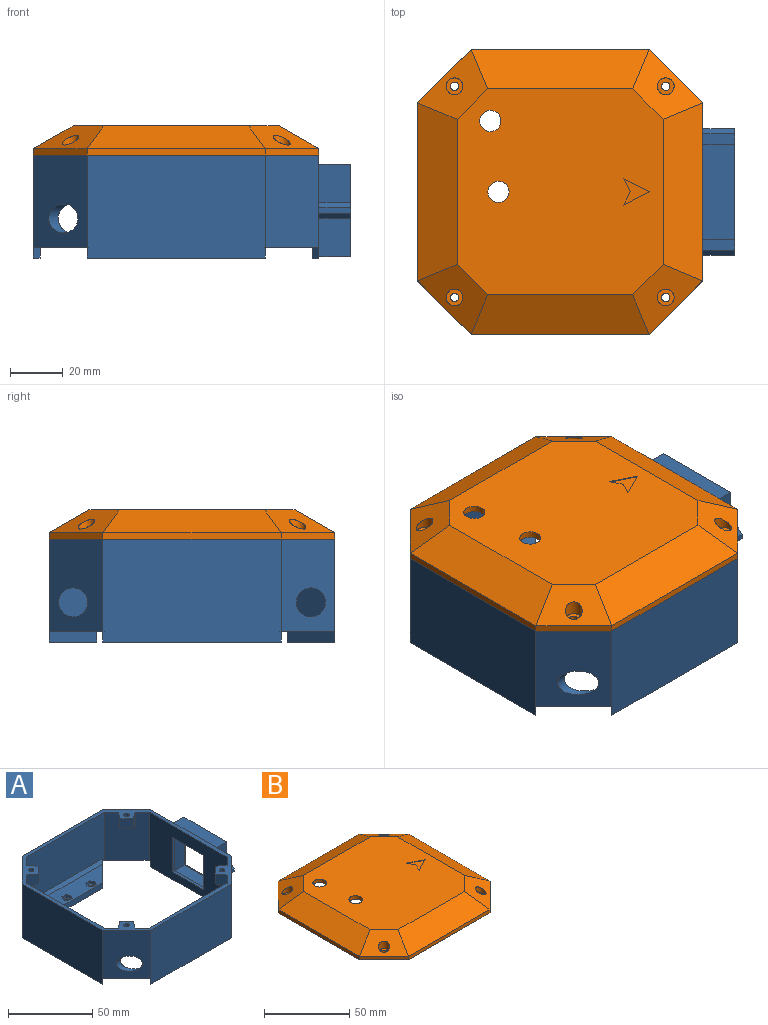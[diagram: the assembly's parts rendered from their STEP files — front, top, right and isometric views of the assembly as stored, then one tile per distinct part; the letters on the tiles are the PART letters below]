
ASSEMBLY  parts=2 mates=1
PART A: 156 faces, bbox 120x108x39 mm
  f0: plane 35x18.85mm, normal (-0.71,0.71,0), area 833.2mm2, adj f14,f20,f25,f28,f143,f144,f153
  f1: plane 35x18.85mm, normal (0.71,0.71,0), area 698.8mm2, adj f12,f20,f27,f28,f29,f131,f132,f141
  f2: plane 35x18.85mm, normal (0.71,-0.71,0), area 698.8mm2, adj f15,f20,f26,f27,f30,f119,f120,f129
  f3: plane 35x18.85mm, normal (-0.71,-0.71,0), area 833.2mm2, adj f13,f20,f25,f26,f107,f108,f117
  f4: cylinder r=1.6mm len=3.2mm, axis (0,0,1), area 20.1mm2, adj f34,f98
  f5: cylinder r=1.6mm len=3.2mm, axis (0,0,1), area 20.1mm2, adj f34,f99
  f6: cylinder r=1.6mm len=3.2mm, axis (0,0,1), area 20.1mm2, adj f40,f85
  f7: cylinder r=1.6mm len=3.2mm, axis (0,0,1), area 20.1mm2, adj f40,f84
  f8: plane 26x2mm, normal (0,0,-1), area 52mm2, adj f9,f10,f25,f51
  f9: plane 25x2mm, normal (0,-1,0), area 50mm2, adj f8,f11,f25,f51
  f10: plane 25x2mm, normal (0,1,0), area 50mm2, adj f8,f11,f25,f51
  f11: plane 26x2mm, normal (0,0,1), area 52mm2, adj f9,f10,f25,f51
  f12: plane 22.82x22.82mm, normal (0,0,-1), area 72.9mm2, adj f1,f24,f27,f28,f32,f44
  f13: plane 22.82x22.82mm, normal (0,0,-1), area 72.9mm2, adj f3,f22,f25,f26,f38,f42
  f14: plane 22.82x22.82mm, normal (0,0,-1), area 72.9mm2, adj f0,f23,f25,f28,f31,f41
  f15: plane 22.82x22.82mm, normal (0,0,-1), area 72.9mm2, adj f2,f21,f26,f27,f37,f45
  f16: plane 67.36x39mm, normal (1,0,0), area 1303.1mm2, adj f20,f22,f23,f41,f42,f43,f57,f58
  f17: plane 67.36x39mm, normal (0,1,0), area 2627.1mm2, adj f20,f21,f22,f37,f38,f40
  f18: plane 67.36x39mm, normal (-1,0,0), area 2627.1mm2, adj f20,f21,f24,f44,f45,f46
  f19: plane 67.36x39mm, normal (0,-1,0), area 2627.1mm2, adj f20,f23,f24,f31,f32,f34
  f20: plane 108x108mm, normal (0,0,1), area 1160.1mm2, adj f0,f1,f2,f3,f16,f17,f18,f19
  f21: plane 35x20.32mm, normal (-0.71,0.71,0), area 871.3mm2, adj f15,f17,f18,f20,f30
  f22: plane 35x20.32mm, normal (0.71,0.71,0), area 1005.7mm2, adj f13,f16,f17,f20
  f23: plane 35x20.32mm, normal (0.71,-0.71,0), area 1005.7mm2, adj f14,f16,f19,f20
  f24: plane 35x20.32mm, normal (-0.71,-0.71,0), area 871.3mm2, adj f12,f18,f19,f20,f29
  f25: plane 65.29x39mm, normal (-1,0,0), area 1884.7mm2, adj f0,f3,f8,f9,f10,f11,f13,f14
  f26: plane 65.29x35mm, normal (0,-1,0), area 2160.5mm2, adj f2,f3,f13,f15,f20,f37,f38,f155
  f27: plane 65.29x39mm, normal (1,0,0), area 2534.7mm2, adj f1,f2,f12,f15,f20,f44,f45,f46
  f28: plane 65.29x35mm, normal (0,1,0), area 2160.5mm2, adj f0,f1,f12,f14,f20,f31,f32,f154
  f29: cylinder r=5.5mm len=14.61mm, axis (-1,0,0), area 122.2mm2, adj f1,f24
  f30: cylinder r=5.5mm len=14.61mm, axis (-1,0,0), area 122.2mm2, adj f2,f21
  f31: plane 18x18mm, normal (0.71,0.71,0), area 104.7mm2, adj f14,f19,f28,f33,f34,f35,f154
  f32: plane 18x18mm, normal (-0.71,0.71,0), area 104.7mm2, adj f12,f19,f28,f33,f34,f35,f154
  f33: plane 31.36x4mm, normal (0,1,0), area 125.5mm2, adj f31,f32,f34,f35
  f34: plane 67.36x18mm, normal (0,0,-1), area 872.4mm2, adj f4,f5,f19,f31,f32,f33
  f35: plane 58.36x13.5mm, normal (0,0,1), area 551.3mm2, adj f31,f32,f33,f92,f93,f94,f95,f96
  f36: plane 58.36x13.5mm, normal (0,0,1), area 551.3mm2, adj f37,f38,f39,f78,f79,f80,f81,f82
  f37: plane 18x18mm, normal (-0.71,-0.71,0), area 104.7mm2, adj f15,f17,f26,f36,f39,f40,f155
  f38: plane 18x18mm, normal (0.71,-0.71,0), area 104.7mm2, adj f13,f17,f26,f36,f39,f40,f155
  f39: plane 31.36x4mm, normal (0,-1,0), area 125.5mm2, adj f36,f37,f38,f40
  f40: plane 67.36x18mm, normal (0,0,-1), area 872.4mm2, adj f6,f7,f17,f37,f38,f39
  f41: plane 4x2.5mm, normal (-0.71,-0.71,0), area 14.1mm2, adj f14,f16,f25,f43
  f42: plane 4x2.5mm, normal (-0.71,0.71,0), area 14.1mm2, adj f13,f16,f25,f43
  f43: plane 67.36x2.5mm, normal (0,0,-1), area 162.2mm2, adj f16,f25,f41,f42
  f44: plane 4x2.5mm, normal (0.71,-0.71,0), area 14.1mm2, adj f12,f18,f27,f46
  f45: plane 4x2.5mm, normal (0.71,0.71,0), area 14.1mm2, adj f15,f18,f27,f46
  f46: plane 67.36x2.5mm, normal (0,0,-1), area 162.2mm2, adj f18,f27,f44,f45
  f47: plane 32x11mm, normal (0,0,-1), area 352mm2, adj f48,f50,f51,f52
  f48: plane 31x11mm, normal (0,1,0), area 341mm2, adj f47,f49,f51,f52
  f49: plane 32x11mm, normal (0,0,1), area 352mm2, adj f48,f50,f51,f52
  f50: plane 31x11mm, normal (0,-1,0), area 341mm2, adj f47,f49,f51,f52
  f51: plane 32x31mm, normal (1,0,0), area 342mm2, adj f8,f9,f10,f11,f47,f48,f49,f50
  f52: plane 34x33mm, normal (1,0,0), area 130mm2, adj f47,f48,f49,f50,f53,f54,f55,f56
  f53: plane 34x1.5mm, normal (0,0,-1), area 51mm2, adj f52,f54,f56,f75
  f54: plane 33x1.5mm, normal (0,1,0), area 49.5mm2, adj f52,f53,f55,f75
  f55: plane 34x1.5mm, normal (0,0,1), area 51mm2, adj f52,f54,f56,f75
  f56: plane 33x1.5mm, normal (0,-1,0), area 49.5mm2, adj f52,f53,f55,f75
  f57: plane 14.5x12mm, normal (0,1,0), area 174mm2, adj f16,f58,f73,f75
  f58: plane 12x4mm, normal (0,0,-1), area 48mm2, adj f16,f57,f59,f75
  f59: plane 12x2mm, normal (0,0.71,-0.71), area 33.9mm2, adj f16,f58,f60,f75
  f60: plane 12x2mm, normal (0,1,0), area 24mm2, adj f16,f59,f61,f75
  f61: plane 12x2mm, normal (0,0.71,0.71), area 33.9mm2, adj f16,f60,f62,f75
  f62: plane 12x4mm, normal (0,0,1), area 48mm2, adj f16,f61,f63,f75
  f63: plane 14.5x12mm, normal (0,1,0), area 174mm2, adj f16,f62,f64,f75
  f64: plane 36x12mm, normal (0,0,1), area 432mm2, adj f16,f63,f65,f75
  f65: plane 14.5x12mm, normal (0,-1,0), area 174mm2, adj f16,f64,f66,f75
  f66: plane 12x4mm, normal (0,0,1), area 48mm2, adj f16,f65,f67,f75
  f67: plane 12x2mm, normal (0,-0.71,0.71), area 33.9mm2, adj f16,f66,f68,f75
  f68: plane 12x2mm, normal (0,-1,0), area 24mm2, adj f16,f67,f69,f75
  f69: plane 12x2mm, normal (0,-0.71,-0.71), area 33.9mm2, adj f16,f68,f70,f75
  f70: plane 12x4mm, normal (0,0,-1), area 48mm2, adj f16,f69,f71,f75
  f71: plane 14.5x12mm, normal (0,-1,0), area 174mm2, adj f16,f70,f73,f75
  f72: cylinder r=1.25mm len=7mm, axis (-1,0,0), area 55mm2, adj f75,f76
  f73: plane 36x12mm, normal (0,0,-1), area 432mm2, adj f16,f57,f71,f75
  f74: cylinder r=1.25mm len=7mm, axis (-1,0,0), area 55mm2, adj f75,f77
  f75: plane 48x35mm, normal (1,0,0), area 192.2mm2, adj f53,f54,f55,f56,f57,f58,f59,f60
  f76: plane 2.5x2.5mm, normal (1,0,0), area 4.9mm2, adj f72
  f77: plane 2.5x2.5mm, normal (1,0,0), area 4.9mm2, adj f74
  f78: plane 3.23x2mm, normal (0,-1,0), area 6.5mm2, adj f36,f79,f83,f84
  f79: plane 2.8x2mm, normal (0.87,-0.5,0), area 6.5mm2, adj f36,f78,f80,f84
  f80: plane 2.8x2mm, normal (0.87,0.5,0), area 6.5mm2, adj f36,f79,f81,f84
  f81: plane 3.23x2mm, normal (0,1,0), area 6.5mm2, adj f36,f80,f82,f84
  f82: plane 2.8x2mm, normal (-0.87,0.5,0), area 6.5mm2, adj f36,f81,f83,f84
  f83: plane 2.8x2mm, normal (-0.87,-0.5,0), area 6.5mm2, adj f36,f78,f82,f84
  f84: plane 6.47x5.6mm, normal (0,0,1), area 19.1mm2, adj f7,f78,f79,f80,f81,f82,f83
  f85: plane 6.47x5.6mm, normal (0,0,1), area 19.1mm2, adj f6,f86,f87,f88,f89,f90,f91
  f86: plane 3.23x2mm, normal (0,-1,0), area 6.5mm2, adj f36,f85,f87,f91
  f87: plane 2.8x2mm, normal (0.87,-0.5,0), area 6.5mm2, adj f36,f85,f86,f88
  f88: plane 2.8x2mm, normal (0.87,0.5,0), area 6.5mm2, adj f36,f85,f87,f89
  f89: plane 3.23x2mm, normal (0,1,0), area 6.5mm2, adj f36,f85,f88,f90
  f90: plane 2.8x2mm, normal (-0.87,0.5,0), area 6.5mm2, adj f36,f85,f89,f91
  f91: plane 2.8x2mm, normal (-0.87,-0.5,0), area 6.5mm2, adj f36,f85,f86,f90
  f92: plane 3.23x2mm, normal (0,-1,0), area 6.5mm2, adj f35,f93,f97,f98
  f93: plane 2.8x2mm, normal (0.87,-0.5,0), area 6.5mm2, adj f35,f92,f94,f98
  f94: plane 2.8x2mm, normal (0.87,0.5,0), area 6.5mm2, adj f35,f93,f95,f98
  f95: plane 3.23x2mm, normal (0,1,0), area 6.5mm2, adj f35,f94,f96,f98
  f96: plane 2.8x2mm, normal (-0.87,0.5,0), area 6.5mm2, adj f35,f95,f97,f98
  f97: plane 2.8x2mm, normal (-0.87,-0.5,0), area 6.5mm2, adj f35,f92,f96,f98
  f98: plane 6.47x5.6mm, normal (0,0,1), area 19.1mm2, adj f4,f92,f93,f94,f95,f96,f97
  f99: plane 6.47x5.6mm, normal (0,0,1), area 19.1mm2, adj f5,f100,f101,f102,f103,f104,f105
  f100: plane 2.8x2mm, normal (0.87,-0.5,0), area 6.5mm2, adj f35,f99,f101,f105
  f101: plane 2.8x2mm, normal (0.87,0.5,0), area 6.5mm2, adj f35,f99,f100,f102
  f102: plane 3.23x2mm, normal (0,1,0), area 6.5mm2, adj f35,f99,f101,f103
  f103: plane 2.8x2mm, normal (-0.87,0.5,0), area 6.5mm2, adj f35,f99,f102,f104
  f104: plane 2.8x2mm, normal (-0.87,-0.5,0), area 6.5mm2, adj f35,f99,f103,f105
  f105: plane 3.23x2mm, normal (0,-1,0), area 6.5mm2, adj f35,f99,f100,f104
  f106: plane 7x5.66mm, normal (-0.71,-0.71,0), area 56mm2, adj f20,f107,f108,f117
  f107: plane 10x5.66mm, normal (0.6,-0.8,0), area 60.1mm2, adj f3,f20,f106,f117
  f108: plane 10x5.66mm, normal (-0.8,0.6,0), area 60.1mm2, adj f3,f20,f106,f117
  f109: plane 3.46x3.12mm, normal (-0.26,0.97,0), area 9.2mm2, adj f110,f114,f116,f117
  f110: plane 2.29x2.29mm, normal (0.71,0.71,0), area 7.3mm2, adj f109,f111,f116,f117
  f111: plane 3.46x3.12mm, normal (0.97,-0.26,0), area 9.2mm2, adj f110,f112,f116,f117
  f112: plane 4.66x3.12mm, normal (0.26,-0.97,0), area 13.1mm2, adj f111,f113,f116,f117
  f113: plane 4.66x2.29mm, normal (-0.71,-0.71,0), area 15.1mm2, adj f112,f114,f116,f117
  f114: plane 4.66x3.12mm, normal (-0.97,0.26,0), area 13.1mm2, adj f109,f113,f116,f117
  f115: cylinder r=1.6mm len=5.25mm, axis (0,0,1), area 52.8mm2, adj f20,f116
  f116: plane 6.25x6.25mm, normal (0,0,-1), area 19.1mm2, adj f109,f110,f111,f112,f113,f114,f115
  f117: plane 11.31x11.31mm, normal (-0.28,-0.28,-0.92), area 39mm2, adj f3,f106,f107,f108,f109,f110,f111,f112
  f118: plane 7x5.66mm, normal (0.71,-0.71,0), area 56mm2, adj f20,f119,f120,f129
  f119: plane 10x5.66mm, normal (-0.6,-0.8,0), area 60.1mm2, adj f2,f20,f118,f129
  f120: plane 10x5.66mm, normal (0.8,0.6,0), area 60.1mm2, adj f2,f20,f118,f129
  f121: plane 3.46x3.12mm, normal (0.26,0.97,0), area 9.2mm2, adj f122,f126,f128,f129
  f122: plane 2.29x2.29mm, normal (-0.71,0.71,0), area 7.3mm2, adj f121,f123,f128,f129
  f123: plane 3.46x3.12mm, normal (-0.97,-0.26,0), area 9.2mm2, adj f122,f124,f128,f129
  f124: plane 4.66x3.12mm, normal (-0.26,-0.97,0), area 13.1mm2, adj f123,f125,f128,f129
  f125: plane 4.66x2.29mm, normal (0.71,-0.71,0), area 15.1mm2, adj f124,f126,f128,f129
  f126: plane 4.66x3.12mm, normal (0.97,0.26,0), area 13.1mm2, adj f121,f125,f128,f129
  f127: cylinder r=1.6mm len=5.25mm, axis (0,0,1), area 52.8mm2, adj f20,f128
  f128: plane 6.25x6.25mm, normal (0,0,-1), area 19.1mm2, adj f121,f122,f123,f124,f125,f126,f127
  f129: plane 11.31x11.31mm, normal (0.28,-0.28,-0.92), area 39mm2, adj f2,f118,f119,f120,f121,f122,f123,f124
  f130: plane 7x5.66mm, normal (0.71,0.71,0), area 56mm2, adj f20,f131,f132,f141
  f131: plane 10x5.66mm, normal (-0.6,0.8,0), area 60.1mm2, adj f1,f20,f130,f141
  f132: plane 10x5.66mm, normal (0.8,-0.6,0), area 60.1mm2, adj f1,f20,f130,f141
  f133: plane 3.46x3.12mm, normal (0.26,-0.97,0), area 9.2mm2, adj f134,f138,f140,f141
  f134: plane 2.29x2.29mm, normal (-0.71,-0.71,0), area 7.3mm2, adj f133,f135,f140,f141
  f135: plane 3.46x3.12mm, normal (-0.97,0.26,0), area 9.2mm2, adj f134,f136,f140,f141
  f136: plane 4.66x3.12mm, normal (-0.26,0.97,0), area 13.1mm2, adj f135,f137,f140,f141
  f137: plane 4.66x2.29mm, normal (0.71,0.71,0), area 15.1mm2, adj f136,f138,f140,f141
  f138: plane 4.66x3.12mm, normal (0.97,-0.26,0), area 13.1mm2, adj f133,f137,f140,f141
  f139: cylinder r=1.6mm len=5.25mm, axis (0,0,1), area 52.8mm2, adj f20,f140
  f140: plane 6.25x6.25mm, normal (0,0,-1), area 19.1mm2, adj f133,f134,f135,f136,f137,f138,f139
  f141: plane 11.31x11.31mm, normal (0.28,0.28,-0.92), area 39mm2, adj f1,f130,f131,f132,f133,f134,f135,f136
  f142: plane 7x5.66mm, normal (-0.71,0.71,0), area 56mm2, adj f20,f143,f144,f153
  f143: plane 10x5.66mm, normal (0.6,0.8,0), area 60.1mm2, adj f0,f20,f142,f153
  f144: plane 10x5.66mm, normal (-0.8,-0.6,0), area 60.1mm2, adj f0,f20,f142,f153
  f145: plane 3.46x3.12mm, normal (-0.26,-0.97,0), area 9.2mm2, adj f146,f150,f152,f153
  f146: plane 2.29x2.29mm, normal (0.71,-0.71,0), area 7.3mm2, adj f145,f147,f152,f153
  f147: plane 3.46x3.12mm, normal (0.97,0.26,0), area 9.2mm2, adj f146,f148,f152,f153
  f148: plane 4.66x3.12mm, normal (0.26,0.97,0), area 13.1mm2, adj f147,f149,f152,f153
  f149: plane 4.66x2.29mm, normal (-0.71,0.71,0), area 15.1mm2, adj f148,f150,f152,f153
  f150: plane 4.66x3.12mm, normal (-0.97,-0.26,0), area 13.1mm2, adj f145,f149,f152,f153
  f151: cylinder r=1.6mm len=5.25mm, axis (0,0,1), area 52.8mm2, adj f20,f152
  f152: plane 6.25x6.25mm, normal (0,0,-1), area 19.1mm2, adj f145,f146,f147,f148,f149,f150,f151
  f153: plane 11.31x11.31mm, normal (-0.28,0.28,-0.92), area 39mm2, adj f0,f142,f143,f144,f145,f146,f147,f148
  f154: plane 62.36x2mm, normal (0,0.71,0.71), area 170.7mm2, adj f28,f31,f32,f35
  f155: plane 62.36x2mm, normal (0,-0.71,0.71), area 170.7mm2, adj f26,f36,f37,f38
PART B: 94 faces, bbox 108.3x108.3x13.3 mm
  f0: cylinder r=3.19mm len=6.38mm, axis (0,0,-1), area 74.2mm2, adj f30,f86
  f1: cylinder r=3.19mm len=6.38mm, axis (0,0,-1), area 73.9mm2, adj f28,f84
  f2: cylinder r=3.19mm len=6.38mm, axis (0,0,-1), area 73.9mm2, adj f26,f82
  f3: cylinder r=3.19mm len=6.38mm, axis (0,0,-1), area 74.2mm2, adj f32,f80
  f4: plane 2x1mm, normal (-1,0,0), area 2mm2, adj f6,f10,f24,f78
  f5: plane 2x1mm, normal (1,0,0), area 2mm2, adj f24,f39,f45,f73
  f6: plane 65.29x13.18mm, normal (-0.49,0,-0.87), area 801.3mm2, adj f4,f13,f36,f43,f46,f75,f76,f78
  f7: plane 2x1mm, normal (0,1,0), area 2mm2, adj f12,f24,f42,f65
  f8: plane 2x1mm, normal (0,-1,0), area 2mm2, adj f11,f24,f44,f60
  f9: plane 5.89x5.89mm, normal (-0.71,0.71,0), area 8.3mm2, adj f13,f24,f34,f58
  f10: plane 5.89x5.89mm, normal (-0.71,-0.71,0), area 8.3mm2, adj f4,f24,f43,f53
  f11: plane 5.89x5.89mm, normal (0.71,-0.71,0), area 8.3mm2, adj f8,f14,f24,f52
  f12: plane 5.89x5.89mm, normal (0.71,0.71,0), area 8.3mm2, adj f7,f15,f24,f49
  f13: plane 24.31x24.31mm, normal (-0.35,0.35,-0.87), area 249mm2, adj f6,f9,f35,f42,f46,f56,f57,f58
  f14: plane 24.31x24.31mm, normal (0.35,-0.35,-0.87), area 249mm2, adj f11,f39,f44,f45,f46,f50,f51,f52
  f15: plane 24.31x24.31mm, normal (0.35,0.35,-0.87), area 249mm2, adj f12,f41,f42,f45,f46,f47,f48,f49
  f16: plane 67.36x2.45mm, normal (0,-1,0), area 165.3mm2, adj f17,f23,f24,f25
  f17: plane 20.32x20.32mm, normal (0.71,-0.71,0), area 70.5mm2, adj f16,f18,f24,f26
  f18: plane 67.36x2.45mm, normal (1,0,0), area 165.3mm2, adj f17,f19,f24,f27
  f19: plane 20.32x20.32mm, normal (0.71,0.71,0), area 70.5mm2, adj f18,f20,f24,f28
  f20: plane 67.36x2.45mm, normal (0,1,0), area 165.3mm2, adj f19,f21,f24,f29
  f21: plane 20.32x20.32mm, normal (-0.71,0.71,0), area 70.5mm2, adj f20,f22,f24,f30
  f22: plane 67.36x2.45mm, normal (-1,0,0), area 165.3mm2, adj f21,f23,f24,f31
  f23: plane 20.32x20.32mm, normal (-0.71,-0.71,0), area 70.5mm2, adj f16,f22,f24,f32
  f24: plane 108x108mm, normal (0,0,-1), area 1160.1mm2, adj f4,f5,f7,f8,f9,f10,f11,f12
  f25: plane 67.36x15.01mm, normal (0,-0.49,0.87), area 1056.3mm2, adj f16,f26,f32,f33
  f26: plane 26.54x26.54mm, normal (0.35,-0.35,0.87), area 352.2mm2, adj f2,f17,f25,f27,f33
  f27: plane 67.36x15.01mm, normal (0.49,0,0.87), area 1056.3mm2, adj f18,f26,f28,f33
  f28: plane 26.54x26.54mm, normal (0.35,0.35,0.87), area 352.2mm2, adj f1,f19,f27,f29,f33
  f29: plane 67.36x15.01mm, normal (0,0.49,0.87), area 1056.3mm2, adj f20,f28,f30,f33
  f30: plane 26.79x26.79mm, normal (-0.35,0.35,0.87), area 352.2mm2, adj f0,f21,f29,f31,f33
  f31: plane 67.36x15.01mm, normal (-0.49,0,0.87), area 1056.3mm2, adj f22,f30,f32,f33
  f32: plane 26.79x26.79mm, normal (-0.35,-0.35,0.87), area 352.2mm2, adj f3,f23,f25,f31,f33
  f33: plane 77.97x77.97mm, normal (0,0,1), area 5676mm2, adj f25,f26,f27,f28,f29,f30,f31,f32
  f34: plane 2x1mm, normal (0,1,0), area 2mm2, adj f9,f24,f42,f68
  f35: plane 5.89x5.89mm, normal (-0.71,0.71,0), area 8.3mm2, adj f13,f24,f36,f56
  f36: plane 2x1mm, normal (-1,0,0), area 2mm2, adj f6,f24,f35,f76
  f37: plane 5.89x5.89mm, normal (-0.71,-0.71,0), area 8.3mm2, adj f24,f38,f43,f55
  f38: plane 2x1mm, normal (0,-1,0), area 2mm2, adj f24,f37,f44,f63
  f39: plane 5.89x5.89mm, normal (0.71,-0.71,0), area 8.3mm2, adj f5,f14,f24,f50
  f40: plane 2x1mm, normal (1,0,0), area 2mm2, adj f24,f41,f45,f70
  f41: plane 5.89x5.89mm, normal (0.71,0.71,0), area 8.3mm2, adj f15,f24,f40,f47
  f42: plane 65.29x13.18mm, normal (0,0.49,-0.87), area 801.3mm2, adj f7,f13,f15,f34,f46,f65,f66,f68
  f43: plane 24.31x24.31mm, normal (-0.35,-0.35,-0.87), area 249mm2, adj f6,f10,f37,f44,f46,f53,f54,f55
  f44: plane 65.29x13.18mm, normal (0,-0.49,-0.87), area 801.3mm2, adj f8,f14,f38,f43,f46,f60,f61,f63
  f45: plane 65.29x13.18mm, normal (0.49,0,-0.87), area 801.3mm2, adj f5,f14,f15,f40,f46,f69,f70,f73
  f46: plane 76.65x76.65mm, normal (0,0,-1), area 5526.6mm2, adj f6,f13,f14,f15,f42,f43,f44,f45
  f47: plane 5.66x4.99mm, normal (-0.6,0.8,0), area 21.2mm2, adj f15,f24,f41,f48
  f48: plane 5.66x5.66mm, normal (0.71,0.71,0), area 39.9mm2, adj f15,f24,f47,f49
  f49: plane 5.66x4.99mm, normal (0.8,-0.6,0), area 21.2mm2, adj f12,f15,f24,f48
  f50: plane 5.66x4.99mm, normal (-0.6,-0.8,0), area 21.2mm2, adj f14,f24,f39,f51
  f51: plane 5.66x5.66mm, normal (0.71,-0.71,0), area 39.9mm2, adj f14,f24,f50,f52
  f52: plane 5.66x4.99mm, normal (0.8,0.6,0), area 21.2mm2, adj f11,f14,f24,f51
  f53: plane 5.66x4.99mm, normal (0.6,-0.8,0), area 21.2mm2, adj f10,f24,f43,f54
  f54: plane 5.66x5.66mm, normal (-0.71,-0.71,0), area 39.9mm2, adj f24,f43,f53,f55
  f55: plane 5.66x4.99mm, normal (-0.8,0.6,0), area 21.2mm2, adj f24,f37,f43,f54
  f56: plane 5.66x4.99mm, normal (0.6,0.8,0), area 21.2mm2, adj f13,f24,f35,f57
  f57: plane 5.66x5.66mm, normal (-0.71,0.71,0), area 39.9mm2, adj f13,f24,f56,f58
  f58: plane 5.66x4.99mm, normal (-0.8,-0.6,0), area 21.2mm2, adj f9,f13,f24,f57
  f59: plane 61.29x2mm, normal (0,1,0), area 122.6mm2, adj f24,f60,f62,f63
  f60: plane 3.85x1.5mm, normal (-1,0,0), area 5.1mm2, adj f8,f44,f59,f61,f62
  f61: plane 61.29x3.85mm, normal (0,-1,0), area 236.2mm2, adj f44,f60,f62,f63
  f62: plane 61.29x1.5mm, normal (0,0,-1), area 91.9mm2, adj f59,f60,f61,f63
  f63: plane 3.85x1.5mm, normal (1,0,0), area 5.1mm2, adj f38,f44,f59,f61,f62
  f64: plane 61.29x2mm, normal (0,-1,0), area 122.6mm2, adj f24,f65,f67,f68
  f65: plane 3.85x1.5mm, normal (-1,0,0), area 5.1mm2, adj f7,f42,f64,f66,f67
  f66: plane 61.29x3.85mm, normal (0,1,0), area 236.2mm2, adj f42,f65,f67,f68
  f67: plane 61.29x1.5mm, normal (0,0,-1), area 91.9mm2, adj f64,f65,f66,f68
  f68: plane 3.85x1.5mm, normal (1,0,0), area 5.1mm2, adj f34,f42,f64,f66,f67
  f69: plane 61.29x3.85mm, normal (1,0,0), area 236.2mm2, adj f45,f70,f72,f73
  f70: plane 3.85x1.5mm, normal (0,-1,0), area 5.1mm2, adj f40,f45,f69,f71,f72
  f71: plane 61.29x2mm, normal (-1,0,0), area 122.6mm2, adj f24,f70,f72,f73
  f72: plane 61.29x1.5mm, normal (0,0,-1), area 91.9mm2, adj f69,f70,f71,f73
  f73: plane 3.85x1.5mm, normal (0,1,0), area 5.1mm2, adj f5,f45,f69,f71,f72
  f74: plane 61.29x2mm, normal (1,0,0), area 122.6mm2, adj f24,f76,f77,f78
  f75: plane 61.29x3.85mm, normal (-1,0,0), area 236.2mm2, adj f6,f76,f77,f78
  f76: plane 3.85x1.5mm, normal (0,-1,0), area 5.1mm2, adj f6,f36,f74,f75,f77
  f77: plane 61.29x1.5mm, normal (0,0,-1), area 91.9mm2, adj f74,f75,f76,f78
  f78: plane 3.85x1.5mm, normal (0,1,0), area 5.1mm2, adj f4,f6,f74,f75,f77
  f79: cylinder r=1.6mm len=3.2mm, axis (0,0,-1), area 19mm2, adj f24,f80
  f80: plane 6.38x6.38mm, normal (0,0,1), area 23.9mm2, adj f3,f79
  f81: cylinder r=1.6mm len=3.2mm, axis (0,0,-1), area 19mm2, adj f24,f82
  f82: plane 6.38x6.38mm, normal (0,0,1), area 23.9mm2, adj f2,f81
  f83: cylinder r=1.6mm len=3.2mm, axis (0,0,-1), area 19mm2, adj f24,f84
  f84: plane 6.38x6.38mm, normal (0,0,1), area 23.9mm2, adj f1,f83
  f85: cylinder r=1.6mm len=3.2mm, axis (0,0,-1), area 19mm2, adj f24,f86
  f86: plane 6.38x6.38mm, normal (0,0,1), area 23.9mm2, adj f0,f85
  f87: plane 10x5mm, normal (-0.45,0.89,0), area 3.4mm2, adj f33,f88,f90,f91
  f88: plane 10x5mm, normal (-0.45,-0.89,0), area 3.4mm2, adj f33,f87,f89,f91
  f89: plane 5x2.47mm, normal (0.9,0.44,0), area 1.7mm2, adj f33,f88,f90,f91
  f90: plane 5x2.47mm, normal (0.9,-0.44,0), area 1.7mm2, adj f33,f87,f89,f91
  f91: plane 10x10mm, normal (0,0,1), area 37.7mm2, adj f87,f88,f89,f90
  f92: cylinder r=4mm len=8mm, axis (0,0,1), area 62.8mm2, adj f33,f46
  f93: cylinder r=4mm len=8mm, axis (0,0,1), area 62.8mm2, adj f33,f46
PLACE A at identity
PLACE B t=(0,0,35)mm
MATE fastened A.f20 <-> B.f24  axis (0,0,1) through (-43.84,-43.84,35)mm
